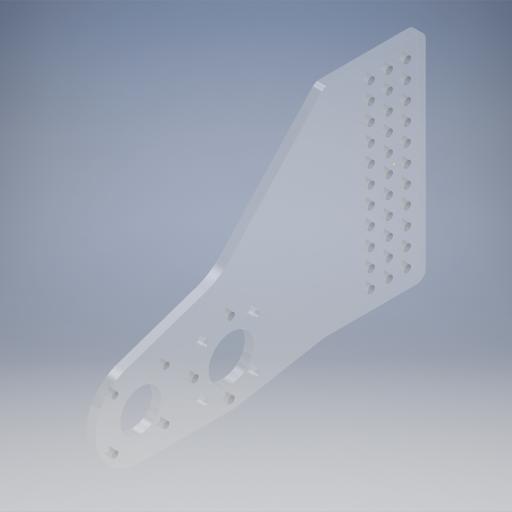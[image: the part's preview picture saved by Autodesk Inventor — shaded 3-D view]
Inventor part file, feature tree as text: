
AUTODESK INVENTOR PART (.ipt)
format: ipt  version: 2024.2 (Build 282272000, 272)  size: 644,608 bytes
history: native  units: in
note: dims shown in document units (in); Inventor stores cm internally (conversion verified against a paired STEP export)
features: sketch x9, extrude x8, projected_geometry x6, other x1
ambient origin geometry x8: Origin, YZ Plane, XZ Plane, XY Plane, X Axis, Y Axis, Z Axis, Center Point
bodies: Solid1 (feature_tree)
feature tree (24):
  extrude  "Extrusion1"  Depth=0.177in
  extrude  "Extrusion2"  Depth=0.707in
  extrude  "Extrusion3"  Depth=0.177in
  extrude  "Extrusion4"  Depth=0.707in
  extrude  "Extrusion5"  Depth=0.707in
  extrude  "Extrusion6"  Depth=0.707in
  sketch  "Sketch8"  dims[d13=0.707in d14=1.0in d15=0.0in]
  extrude  "Extrusion7"  Depth=1.0in TaperAngle=0.0deg
  extrude  "Extrusion8"  Depth=0.196in
  sketch  "Sketch1"  dims[d0=1.0in d1=0.0in d2=0.177in]
  projected_geometry  "Projected Loop1"
  sketch  "Sketch3"  dims[d3=0.707in d4=0.707in]
  projected_geometry  "Projected Loop2"
  sketch  "Sketch4"  dims[d5=0.177in d6=0.177in]
  projected_geometry  "Projected Loop3"
  sketch  "Sketch5"  dims[d7=0.177in d8=0.707in]
  projected_geometry  "Projected Loop4"
  sketch  "Sketch6"  dims[d9=0.707in d10=0.707in]
  projected_geometry  "Projected Loop5"
  sketch  "Sketch7"  dims[d11=0.707in d12=0.707in]
  sketch  "Sketch9"  dims[d16=1.414in d17=0.196in]
  projected_geometry  "Projected Loop6"
  sketch  "Sketch10"  dims[d18=0.0in d19=-1.0in d20=3.1496in d22=360.0deg d24=0.6875in d25=0.0in d26=0.6875in d27=0.0in d28=1.0in d29=0.0in d30=0.196in d31=0.5in d32=0.5in d33=4.3307in d35=0.5in d36=1.1811in d38=0.5in d41=1.0in d42=0.0in d43=1.125in d44=0.177in d45=0.177in d46=0.707in d47=0.707in d48=0.707in d49=0.707in d50=0.707in d51=0.875in d52=0.0in d53=0.875in d54=0.0in]
  other  "Part 2"
